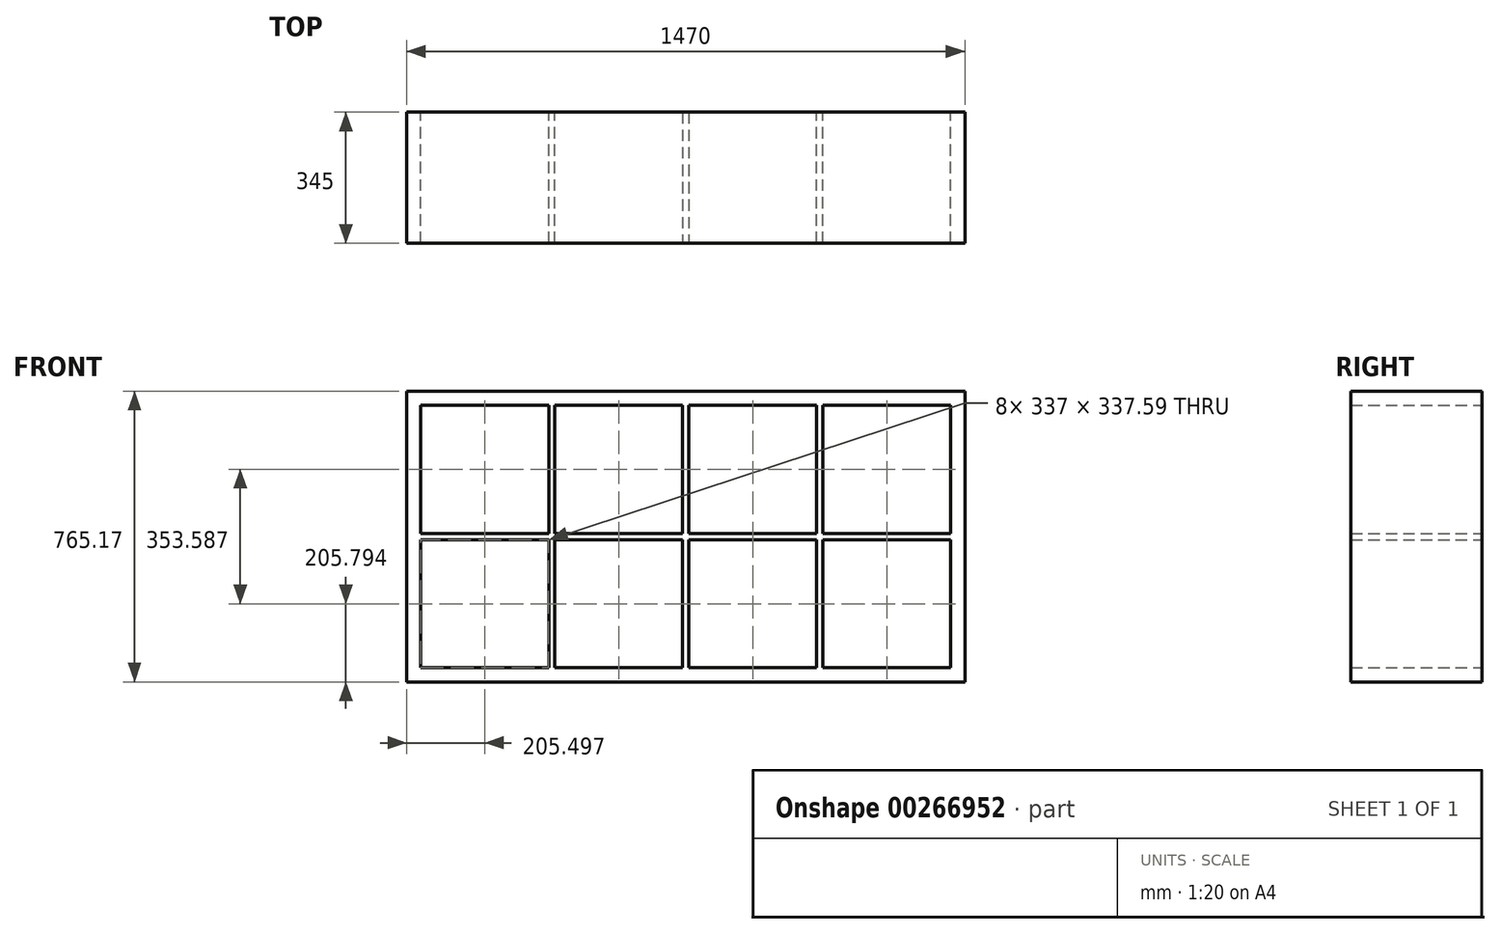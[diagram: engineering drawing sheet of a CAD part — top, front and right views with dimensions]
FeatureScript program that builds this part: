
annotation { "Feature Type Name" : "Feature", "Feature Type Description" : "" }
export const myFeature = defineFeature(function(context is Context, id is Id, definition is map)
    precondition{}
    {
        {
            var Q0;
            Q0=qCreatedBy(makeId("Front.planeOp"),FACE);
            var sketch = newSketch(context, id + "F0", { "sketchPlane" : qUnion([Q0])});
            skLineSegment(sketch, "E0.bottom", {"start": v(-38.6, 280.62) * mm, "end": v(-1.6, 280.62) * mm});
            skLineSegment(sketch, "E0.top", {"start": v(-38.6, -101.97) * mm, "end": v(-1.6, -101.97) * mm});
            skLineSegment(sketch, "E0.left", {"start": v(-38.6, 280.62) * mm, "end": v(-38.6, -101.97) * mm});
            skLineSegment(sketch, "E0.right", {"start": v(-1.6, 280.62) * mm, "end": v(-1.6, -101.97) * mm});
            skSolve(sketch);
        }
        {
            var Q0;
            Q0 = qSketchRegion(id + "F0", true);
            extrude(context, id + "F1", {"entities" : qUnion([Q0]), "depth" : 345 * mm});
        }
        {
            var Q0;
            Q0=makeQuery(id+"F1.opExtrude","SWEPT_FACE",FACE,{"disambiguationData":[OSD([sQuery(id+"F0.wireOp",EDGE,"E0.right")])]});
            var sketch = newSketch(context, id + "F2", { "sketchPlane" : qUnion([Q0])});
            skLineSegment(sketch, "E1.bottom", {"start": v(-345, -101.97) * mm, "end": v(0, -101.97) * mm});
            skLineSegment(sketch, "E1.top", {"start": v(-345, -64.97) * mm, "end": v(0, -64.97) * mm});
            skLineSegment(sketch, "E1.left", {"start": v(-345, -101.97) * mm, "end": v(-345, -64.97) * mm});
            skLineSegment(sketch, "E1.right", {"start": v(0, -101.97) * mm, "end": v(0, -64.97) * mm});
            skSolve(sketch);
        }
        {
            var Q0;
            Q0 = qSketchRegion(id + "F2", true);
            extrude(context, id + "F3", {"entities" : qUnion([Q0]), "operationType" : NewBodyOperationType.ADD, "depth" : 698 * mm});
        }
        {
            var Q0;
            Q0=makeQuery(id+"F3.opExtrude","SWEPT_FACE",FACE,{"disambiguationData":[OSD([sQuery(id+"F2.wireOp",EDGE,"E1.top")])]});
            var sketch = newSketch(context, id + "F4", { "sketchPlane" : qUnion([Q0])});
            skLineSegment(sketch, "E2.bottom", {"start": v(335.4, -345) * mm, "end": v(351.4, -345) * mm});
            skLineSegment(sketch, "E2.top", {"start": v(335.4, 0) * mm, "end": v(351.4, 0) * mm});
            skLineSegment(sketch, "E2.left", {"start": v(335.4, -345) * mm, "end": v(335.4, 0) * mm});
            skLineSegment(sketch, "E2.right", {"start": v(351.4, -345) * mm, "end": v(351.4, 0) * mm});
            skLineSegment(sketch, "E3.bottom", {"start": v(696.4, 0) * mm, "end": v(688.4, 0) * mm});
            skLineSegment(sketch, "E3.top", {"start": v(696.4, -345) * mm, "end": v(688.4, -345) * mm});
            skLineSegment(sketch, "E3.left", {"start": v(696.4, 0) * mm, "end": v(696.4, -345) * mm});
            skLineSegment(sketch, "E3.right", {"start": v(688.4, 0) * mm, "end": v(688.4, -345) * mm});
            skSolve(sketch);
        }
        {
            var Q0;
            Q0=makeQuery(id+"F1.opExtrude","SWEPT_FACE",FACE,{"disambiguationData":[OSD([sQuery(id+"F0.wireOp",EDGE,"E0.right")])]});
            var sketch = newSketch(context, id + "F7", { "sketchPlane" : qUnion([Q0])});
            skLineSegment(sketch, "E4.bottom", {"start": v(-345, 280.62) * mm, "end": v(0, 280.62) * mm});
            skLineSegment(sketch, "E4.top", {"start": v(-345, 272.62) * mm, "end": v(0, 272.62) * mm});
            skLineSegment(sketch, "E4.left", {"start": v(-345, 280.62) * mm, "end": v(-345, 272.62) * mm});
            skLineSegment(sketch, "E4.right", {"start": v(0, 280.62) * mm, "end": v(0, 272.62) * mm});
            skSolve(sketch);
        }
        {
            var Q0;
            Q0 = qSketchRegion(id + "F7", true);
            extrude(context, id + "F8", {"entities" : qUnion([Q0]), "operationType" : NewBodyOperationType.ADD, "depth" : 698 * mm});
        }
        {
            var Q0;
            Q0=makeQuery(id+"F4.imprint","IMPRINT",FACE,{"disambiguationData":[TD([[makeQuery(id+"F4.imprint","IMPRINT",EDGE,{"derivedFrom":sQuery(id+"F4.wireOp",EDGE,"E2.bottom")}),-1.0]])]});
            var Q1;
            Q1=makeQuery(id+"F4.imprint","IMPRINT",FACE,{"disambiguationData":[TD([[makeQuery(id+"F4.imprint","IMPRINT",EDGE,{"derivedFrom":sQuery(id+"F4.wireOp",EDGE,"E3.bottom")}),1.0]])]});
            extrude(context, id + "F5", {"entities" : qUnion([Q0, Q1]), "operationType" : NewBodyOperationType.ADD, "endBound" : BoundingType.UP_TO_NEXT, "depth" : 25 * mm});
        }
        {
            var Q0;
            Q0=makeQuery(id+"F1.opExtrude","SWEPT_BODY",BODY,{"disambiguationData":[OSD([sQuery(id+"F0.wireOp",EDGE,"E0.bottom"),sQuery(id+"F0.wireOp",EDGE,"E0.top"),sQuery(id+"F0.wireOp",EDGE,"E0.left"),sQuery(id+"F0.wireOp",EDGE,"E0.right")])]});
            var Q1;
            Q1=makeQuery(id+"F8.boolean.opBoolean","MERGE",FACE,{"derivedFrom":[makeQuery(id+"F1.opExtrude","SWEPT_FACE",FACE,{"disambiguationData":[OSD([sQuery(id+"F0.wireOp",EDGE,"E0.bottom")])]}),makeQuery(id+"F8.opExtrude","SWEPT_FACE",FACE,{"disambiguationData":[OSD([sQuery(id+"F7.wireOp",EDGE,"E4.bottom")])]})]});
            mirror(context, id + "F9", {"operationType" : NewBodyOperationType.ADD, "entities" : qUnion([Q0]), "mirrorPlane" : qUnion([Q1])});
        }
        {
            var Q0;
            Q0=makeQuery(id+"F1.opExtrude","SWEPT_BODY",BODY,{"disambiguationData":[OSD([sQuery(id+"F0.wireOp",EDGE,"E0.bottom"),sQuery(id+"F0.wireOp",EDGE,"E0.top"),sQuery(id+"F0.wireOp",EDGE,"E0.left"),sQuery(id+"F0.wireOp",EDGE,"E0.right")])]});
            var Q1;
            {var subQ0=makeQuery(id+"F5.boolean.opBoolean","MERGE",FACE,{"derivedFrom":[makeQuery(id+"F3.opExtrude","CAP_FACE",FACE,{"disambiguationData":[OSD([sQuery(id+"F2.wireOp",EDGE,"E1.bottom"),sQuery(id+"F2.wireOp",EDGE,"E1.top"),sQuery(id+"F2.wireOp",EDGE,"E1.left"),sQuery(id+"F2.wireOp",EDGE,"E1.right")])],"isStart":false}),makeQuery(id+"F8.opExtrude","CAP_FACE",FACE,{"disambiguationData":[OSD([sQuery(id+"F7.wireOp",EDGE,"E4.bottom"),sQuery(id+"F7.wireOp",EDGE,"E4.top"),sQuery(id+"F7.wireOp",EDGE,"E4.left"),sQuery(id+"F7.wireOp",EDGE,"E4.right")])],"isStart":false}),makeQuery(id+"F5.opExtrude","SWEPT_FACE",FACE,{"disambiguationData":[OSD([sQuery(id+"F4.wireOp",EDGE,"E3.left")])]})]});Q1=makeQuery(id+"F9.boolean.opBoolean","MERGE",FACE,{"derivedFrom":[subQ0,makeQuery(id+"F9.opPattern","COPY",FACE,{"derivedFrom":subQ0,"instanceName":"1"})]});}
            mirror(context, id + "F6", {"operationType" : NewBodyOperationType.ADD, "entities" : qUnion([Q0]), "mirrorPlane" : qUnion([Q1])});
        }
    });
